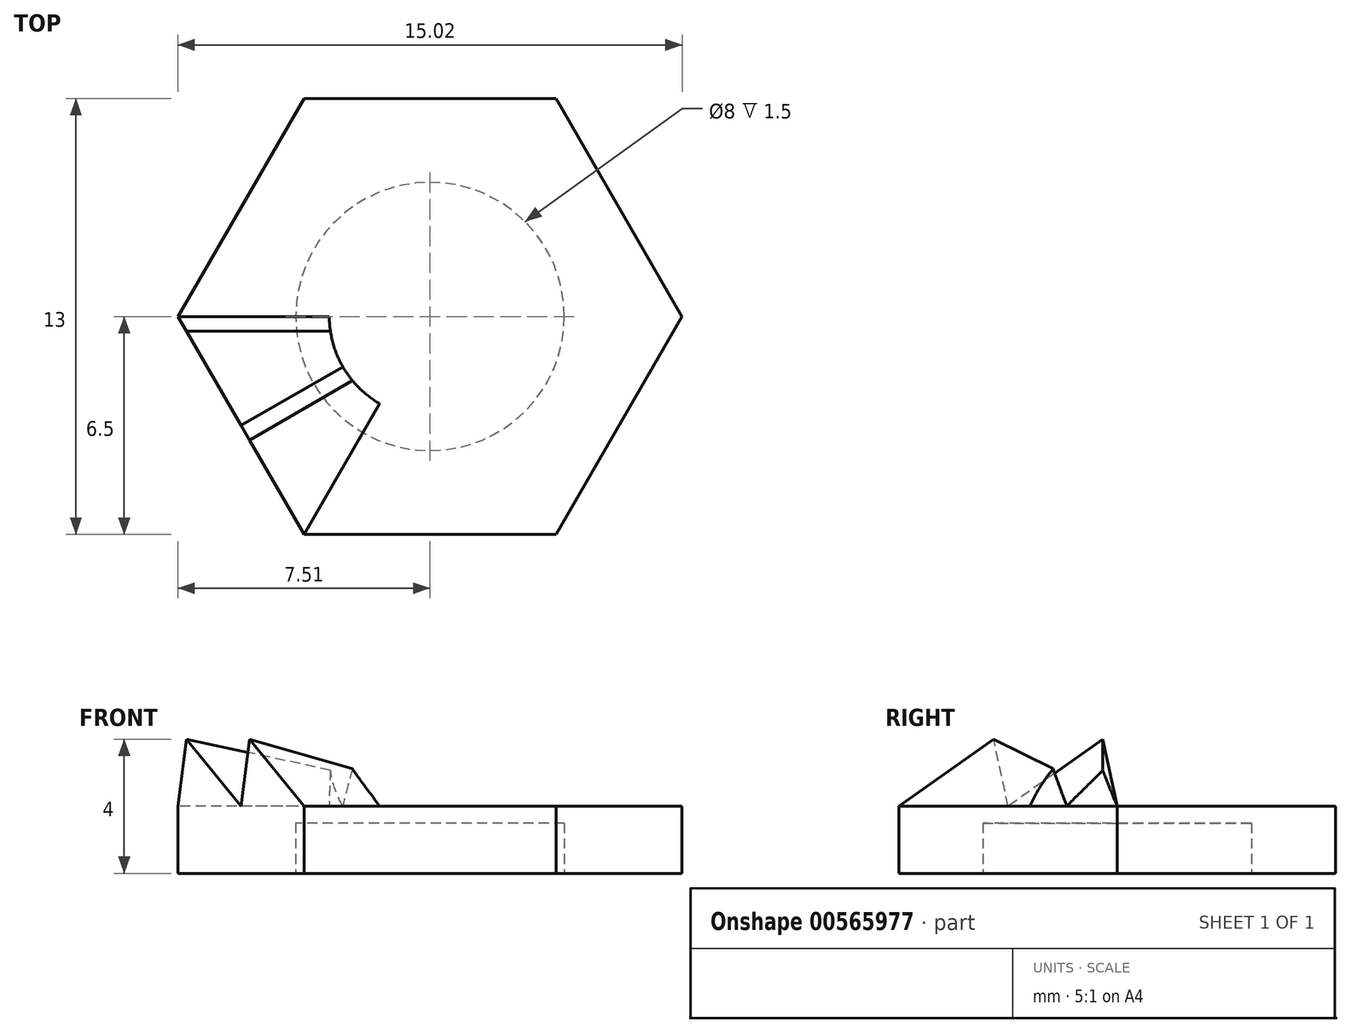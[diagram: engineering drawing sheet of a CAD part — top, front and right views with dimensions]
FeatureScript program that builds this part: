
annotation { "Feature Type Name" : "Feature", "Feature Type Description" : "" }
export const myFeature = defineFeature(function(context is Context, id is Id, definition is map)
    precondition{}
    {
        {
            var Q0;
            Q0=qCreatedBy(makeId("Top.planeOp"),FACE);
            var sketch = newSketch(context, id + "F0", { "sketchPlane" : qUnion([Q0])});
            skCircle(sketch, "E0.cCircle", {"center": v(0, 0) * mm, "radius": 6.5 * mm, "construction": true});
            skLineSegment(sketch, "E0.0", {"start": v(-3.75, 6.5) * mm, "end": v(3.75, 6.5) * mm});
            skLineSegment(sketch, "E0.1", {"start": v(3.75, 6.5) * mm, "end": v(7.5, 0) * mm});
            skLineSegment(sketch, "E0.2", {"start": v(7.5, 0) * mm, "end": v(3.75, -6.5) * mm});
            skLineSegment(sketch, "E0.3", {"start": v(3.75, -6.5) * mm, "end": v(-3.75, -6.5) * mm});
            skLineSegment(sketch, "E0.4", {"start": v(-3.75, -6.5) * mm, "end": v(-7.5, 0) * mm});
            skLineSegment(sketch, "E0.5", {"start": v(-7.5, 0) * mm, "end": v(-3.75, 6.5) * mm});
            skPoint(sketch, "E0.0.midPoint", {"position": v(0, 6.5) * mm});
            skSolve(sketch);
        }
        {
            var Q0;
            Q0=makeQuery(id+"F0.imprint","IMPRINT",FACE,{"disambiguationData":[TD([[makeQuery(id+"F0.imprint","IMPRINT",EDGE,{"derivedFrom":sQuery(id+"F0.wireOp",EDGE,"E0.0")}),-1.0]])]});
            extrude(context, id + "F1", {"entities" : qUnion([Q0]), "depth" : 2 * mm, "offsetDistance" : 25 * mm});
        }
        {
            var Q0;
            Q0=makeQuery(id+"F1.opExtrude","SWEPT_FACE",FACE,{"disambiguationData":[OSD([sQuery(id+"F0.wireOp",EDGE,"E0.4")])]});
            cPlane(context, id + "F2", {"entities" : qUnion([Q0]), "cplaneType" : CPlaneType.OFFSET, "offset" : 4 * mm, "oppositeDirection" : true, "width" : 150 * mm, "height" : 150 * mm});
        }
        {
            var Q0;
            Q0=makeQuery(id+"F1.opExtrude","SWEPT_FACE",FACE,{"disambiguationData":[OSD([sQuery(id+"F0.wireOp",EDGE,"E0.4")])]});
            var sketch = newSketch(context, id + "F3", { "sketchPlane" : qUnion([Q0])});
            skLineSegment(sketch, "E1", {"start": v(-3.75, 2) * mm, "end": v(-3.25, 4) * mm});
            skLineSegment(sketch, "E2", {"start": v(-3.25, 4) * mm, "end": v(0, 2) * mm});
            skLineSegment(sketch, "E3", {"start": v(0, 2) * mm, "end": v(-3.75, 2) * mm});
            skLineSegment(sketch, "E4", {"start": v(0, 2) * mm, "end": v(0.5, 4) * mm});
            skLineSegment(sketch, "E5", {"start": v(0.5, 4) * mm, "end": v(3.75, 2) * mm});
            skLineSegment(sketch, "E6", {"start": v(3.75, 2) * mm, "end": v(0, 2) * mm});
            skSolve(sketch);
        }
        {
            var Q0;
            Q0=makeQuery(id+"F1.opExtrude","CAP_FACE",FACE,{"disambiguationData":[OSD([sQuery(id+"F0.wireOp",EDGE,"E0.0"),sQuery(id+"F0.wireOp",EDGE,"E0.1"),sQuery(id+"F0.wireOp",EDGE,"E0.2"),sQuery(id+"F0.wireOp",EDGE,"E0.3"),sQuery(id+"F0.wireOp",EDGE,"E0.4"),sQuery(id+"F0.wireOp",EDGE,"E0.5")])],"isStart":false});
            var sketch = newSketch(context, id + "F4", { "sketchPlane" : qUnion([Q0])});
            skLineSegment(sketch, "E7", {"start": v(-5.63, -3.25) * mm, "end": v(0, 0) * mm, "construction": true});
            skLineSegment(sketch, "E8", {"start": v(-3.75, -6.5) * mm, "end": v(0, 0) * mm, "construction": true});
            skSolve(sketch);
        }
        {
            var Q0;
            Q0=qCreatedBy(id+"F2.planeOp",FACE);
            var sketch = newSketch(context, id + "F5", { "sketchPlane" : qUnion([Q0])});
            skLineSegment(sketch, "E9", {"start": v(-1.44, 2) * mm, "end": v(-0.94, 3) * mm});
            skLineSegment(sketch, "E10", {"start": v(-0.94, 3) * mm, "end": v(0, 2) * mm});
            skLineSegment(sketch, "E11", {"start": v(0, 2) * mm, "end": v(-1.44, 2) * mm});
            skLineSegment(sketch, "E12", {"start": v(0, 2) * mm, "end": v(0.5, 3) * mm});
            skLineSegment(sketch, "E13", {"start": v(0.5, 3) * mm, "end": v(1.44, 2) * mm});
            skLineSegment(sketch, "E14", {"start": v(1.44, 2) * mm, "end": v(0, 2) * mm});
            skSolve(sketch);
        }
        {
            var Q1;
            Q1=makeQuery(id+"F5.imprint","IMPRINT",FACE,{"disambiguationData":[TD([[makeQuery(id+"F5.imprint","IMPRINT",EDGE,{"derivedFrom":sQuery(id+"F5.wireOp",EDGE,"E9")}),-1.0]])]});
            var Q2;
            Q2=makeQuery(id+"F3.imprint","IMPRINT",FACE,{"disambiguationData":[TD([[makeQuery(id+"F3.imprint","IMPRINT",EDGE,{"derivedFrom":sQuery(id+"F3.wireOp",EDGE,"E1")}),-1.0]])]});
            loft(context, id + "F6", {"operationType" : NewBodyOperationType.ADD, "sheetProfilesArray" : [{ "sheetProfileEntities" : qUnion([Q1]) }, { "sheetProfileEntities" : qUnion([Q2]) }]});
        }
        {
            var Q1;
            Q1=makeQuery(id+"F5.imprint","IMPRINT",FACE,{"disambiguationData":[TD([[makeQuery(id+"F5.imprint","IMPRINT",EDGE,{"derivedFrom":sQuery(id+"F5.wireOp",EDGE,"E12")}),-1.0]])]});
            var Q2;
            Q2=makeQuery(id+"F3.imprint","IMPRINT",FACE,{"disambiguationData":[TD([[makeQuery(id+"F3.imprint","IMPRINT",EDGE,{"derivedFrom":sQuery(id+"F3.wireOp",EDGE,"E4")}),-1.0]])]});
            loft(context, id + "F7", {"operationType" : NewBodyOperationType.ADD, "sheetProfilesArray" : [{ "sheetProfileEntities" : qUnion([Q1]) }, { "sheetProfileEntities" : qUnion([Q2]) }]});
        }
        {
            var Q0;
            Q0=qCreatedBy(makeId("Top.planeOp"),FACE);
            var sketch = newSketch(context, id + "F8", { "sketchPlane" : qUnion([Q0])});
            skCircle(sketch, "E15", {"center": v(0, 0) * mm, "radius": 4 * mm});
            skSolve(sketch);
        }
        {
            var Q0;
            Q0=makeQuery(id+"F8.imprint","IMPRINT",FACE,{"disambiguationData":[TD([[makeQuery(id+"F8.imprint","IMPRINT",EDGE,{"derivedFrom":sQuery(id+"F8.wireOp",EDGE,"E15")}),1.0]])]});
            extrude(context, id + "F9", {"entities" : qUnion([Q0]), "operationType" : NewBodyOperationType.REMOVE, "depth" : 1.5 * mm, "offsetDistance" : 25 * mm});
        }
        {
            var Q0;
            Q0=makeQuery(id+"F1.opExtrude","CAP_FACE",FACE,{"disambiguationData":[OSD([sQuery(id+"F0.wireOp",EDGE,"E0.0"),sQuery(id+"F0.wireOp",EDGE,"E0.1"),sQuery(id+"F0.wireOp",EDGE,"E0.2"),sQuery(id+"F0.wireOp",EDGE,"E0.3"),sQuery(id+"F0.wireOp",EDGE,"E0.4"),sQuery(id+"F0.wireOp",EDGE,"E0.5")])],"isStart":false});
            var sketch = newSketch(context, id + "F10", { "sketchPlane" : qUnion([Q0])});
            skCircle(sketch, "E16", {"center": v(0, 0) * mm, "radius": 3 * mm});
            skSolve(sketch);
        }
        {
            var Q0;
            Q0 = qSketchRegion(id + "F10", true);
            extrude(context, id + "F11", {"entities" : qUnion([Q0]), "operationType" : NewBodyOperationType.REMOVE, "endBound" : BoundingType.THROUGH_ALL, "depth" : 25 * mm, "offsetDistance" : 25 * mm});
        }
    });
